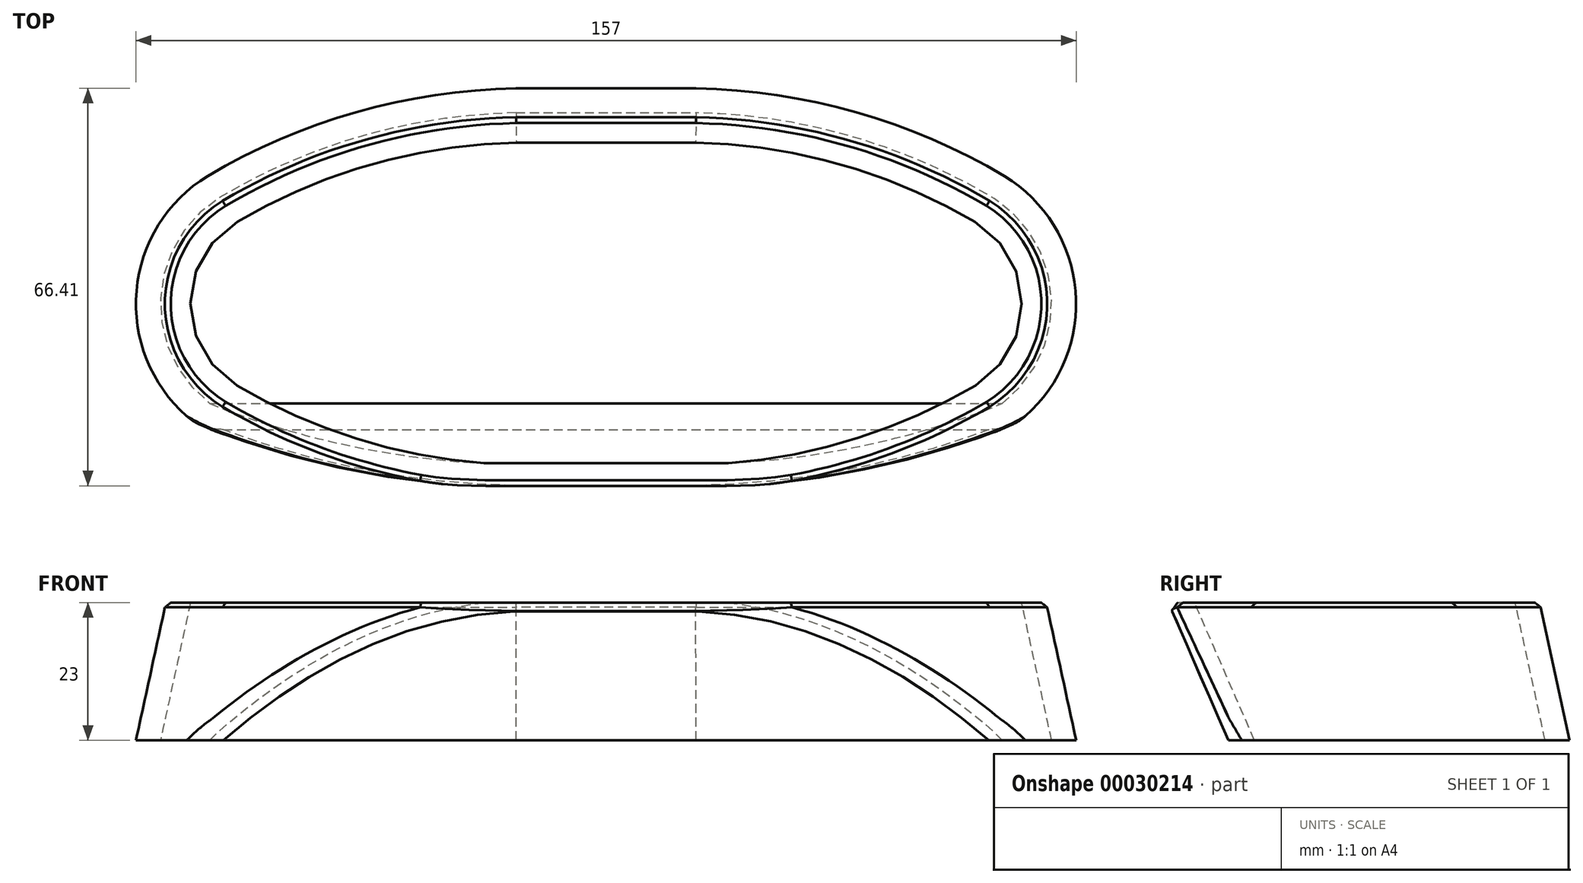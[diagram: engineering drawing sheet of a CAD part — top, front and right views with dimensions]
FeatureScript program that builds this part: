
annotation { "Feature Type Name" : "Feature", "Feature Type Description" : "" }
export const myFeature = defineFeature(function(context is Context, id is Id, definition is map)
    precondition{}
    {
        {
            var Q0;
            Q0=qCreatedBy(makeId("Top.planeOp"),FACE);
            var sketch = newSketch(context, id + "F0", { "sketchPlane" : qUnion([Q0])});
            skLineSegment(sketch, "E0.rect.bottom", {"start": v(-15, -31) * mm, "end": v(15, -31) * mm, "construction": true});
            skLineSegment(sketch, "E0.rect.top", {"start": v(-15, 31) * mm, "end": v(15, 31) * mm, "construction": true});
            skLineSegment(sketch, "E0.rect.left", {"start": v(-15, -31) * mm, "end": v(-15, 31) * mm, "construction": true});
            skLineSegment(sketch, "E0.rect.right", {"start": v(15, -31) * mm, "end": v(15, 31) * mm, "construction": true});
            skPoint(sketch, "E0.rect.middle", {"position": v(0, 0) * mm});
            skLineSegment(sketch, "E1", {"start": v(-53.5, 0) * mm, "end": v(0, 0) * mm, "construction": true});
            skArc(sketch, "E2", {"start": v(-63.95, 17.05) * mm, "mid": v(-73.5, 0) * mm, "end": v(-63.95, -17.05) * mm, "construction": true});
            skLineSegment(sketch, "E3", {"start": v(-15, 31) * mm, "end": v(-58.67, 19.32) * mm, "construction": true});
            skArc(sketch, "E4", {"start": v(-63.95, -17.05) * mm, "mid": v(-40.38, -27.2) * mm, "end": v(-15, -31) * mm, "construction": true});
            skArc(sketch, "E5.MirrorCS", {"start": v(-63.95, 17.05) * mm, "mid": v(-40.38, 27.2) * mm, "end": v(-15, 31) * mm, "construction": true});
            skArc(sketch, "E6.MirrorCS", {"start": v(63.95, 17.05) * mm, "mid": v(40.38, 27.2) * mm, "end": v(15, 31) * mm, "construction": true});
            skArc(sketch, "E7.MirrorCS", {"start": v(63.95, 17.05) * mm, "mid": v(73.5, 0) * mm, "end": v(63.95, -17.05) * mm, "construction": true});
            skArc(sketch, "E8.MirrorCS", {"start": v(63.95, -17.05) * mm, "mid": v(40.38, -27.2) * mm, "end": v(15, -31) * mm, "construction": true});
            skArc(sketch, "E9.0", {"start": v(-66.53, 21.34) * mm, "mid": v(-78.5, 0) * mm, "end": v(-66.53, -21.34) * mm});
            skArc(sketch, "E9.1", {"start": v(-66.53, -21.34) * mm, "mid": v(-41.74, -32) * mm, "end": v(-15.05, -36) * mm});
            skLineSegment(sketch, "E9.2", {"start": v(-15.05, -36) * mm, "end": v(15.05, -36) * mm});
            skArc(sketch, "E9.3", {"start": v(66.53, -21.34) * mm, "mid": v(41.74, -32) * mm, "end": v(15.05, -36) * mm});
            skArc(sketch, "E9.4", {"start": v(66.53, 21.34) * mm, "mid": v(78.5, 0) * mm, "end": v(66.53, -21.34) * mm});
            skArc(sketch, "E9.5", {"start": v(-66.53, 21.34) * mm, "mid": v(-41.74, 32) * mm, "end": v(-15.05, 36) * mm});
            skArc(sketch, "E9.6", {"start": v(66.53, 21.34) * mm, "mid": v(41.74, 32) * mm, "end": v(15.05, 36) * mm});
            skLineSegment(sketch, "E9.7", {"start": v(-15.05, 36) * mm, "end": v(15.05, 36) * mm});
            skSolve(sketch);
        }
        {
            var Q0;
            Q0=qCreatedBy(makeId("Top.planeOp"),FACE);
            cPlane(context, id + "F1", {"entities" : qUnion([Q0]), "cplaneType" : CPlaneType.OFFSET, "offset" : 23 * mm, "width" : 150 * mm, "height" : 150 * mm});
        }
        {
            var Q0;
            Q0=qCreatedBy(id+"F1.planeOp",FACE);
            var sketch = newSketch(context, id + "F2", { "sketchPlane" : qUnion([Q0])});
            skLineSegment(sketch, "E10.rect.bottom", {"start": v(-15, -31) * mm, "end": v(15, -31) * mm});
            skLineSegment(sketch, "E10.rect.top", {"start": v(-15, 31) * mm, "end": v(15, 31) * mm});
            skLineSegment(sketch, "E10.rect.left", {"start": v(-15, -31) * mm, "end": v(-15, 31) * mm, "construction": true});
            skLineSegment(sketch, "E10.rect.right", {"start": v(15, -31) * mm, "end": v(15, 31) * mm, "construction": true});
            skPoint(sketch, "E10.rect.middle", {"position": v(0, 0) * mm});
            skLineSegment(sketch, "E11", {"start": v(-53.5, 0) * mm, "end": v(0, 0) * mm, "construction": true});
            skArc(sketch, "E12", {"start": v(-63.95, 17.05) * mm, "mid": v(-73.5, 0) * mm, "end": v(-63.95, -17.05) * mm});
            skLineSegment(sketch, "E13", {"start": v(-15, 31) * mm, "end": v(-58.67, 19.32) * mm, "construction": true});
            skArc(sketch, "E14", {"start": v(-63.95, -17.05) * mm, "mid": v(-40.38, -27.2) * mm, "end": v(-15, -31) * mm});
            skArc(sketch, "E15.MirrorCS", {"start": v(-63.95, 17.05) * mm, "mid": v(-40.38, 27.2) * mm, "end": v(-15, 31) * mm});
            skArc(sketch, "E16.MirrorCS", {"start": v(63.95, 17.05) * mm, "mid": v(40.38, 27.2) * mm, "end": v(15, 31) * mm});
            skArc(sketch, "E17.MirrorCS", {"start": v(63.95, 17.05) * mm, "mid": v(73.5, 0) * mm, "end": v(63.95, -17.05) * mm});
            skArc(sketch, "E18.MirrorCS", {"start": v(63.95, -17.05) * mm, "mid": v(40.38, -27.2) * mm, "end": v(15, -31) * mm});
            skSolve(sketch);
        }
        {
            var Q0;
            Q0=makeQuery(id+"F0.imprint","IMPRINT",FACE,{"disambiguationData":[TD([[makeQuery(id+"F0.imprint","IMPRINT",EDGE,{"derivedFrom":sQuery(id+"F0.wireOp",EDGE,"E9.0")}),1.0]])]});
            var Q1;
            Q1=makeQuery(id+"F2.imprint","IMPRINT",FACE,{"disambiguationData":[TD([[makeQuery(id+"F2.imprint","IMPRINT",EDGE,{"derivedFrom":sQuery(id+"F2.wireOp",EDGE,"E10.rect.bottom")}),1.0]])]});
            loft(context, id + "F3", {"sheetProfilesArray" : [{ "sheetProfileEntities" : qUnion([Q0]) }, { "sheetProfileEntities" : qUnion([Q1]) }]});
        }
        {
            var Q0;
            Q0=qCreatedBy(makeId("Right.planeOp"),FACE);
            var sketch = newSketch(context, id + "F4", { "sketchPlane" : qUnion([Q0])});
            skLineSegment(sketch, "E19", {"start": v(-31, 23) * mm, "end": v(-21, 0) * mm});
            skLineSegment(sketch, "E20", {"start": v(-21, 0) * mm, "end": v(-51, 0) * mm});
            skLineSegment(sketch, "E21", {"start": v(-51, 0) * mm, "end": v(-31, 23) * mm});
            skSolve(sketch);
        }
        {
            var Q0;
            Q0 = qSketchRegion(id + "F4", true);
            extrude(context, id + "F5", {"entities" : qUnion([Q0]), "operationType" : NewBodyOperationType.REMOVE, "oppositeDirection" : true, "depth" : 70 * mm, "hasSecondDirection" : true, "secondDirectionOppositeDirection" : false, "secondDirectionDepth" : 70 * mm});
        }
        {
            var Q0;
            Q0=makeQuery(id+"F3.opLoft","CAP_FACE",FACE,{"disambiguationData":[OSD([makeQuery(id+"F2.imprint","IMPRINT",FACE,{"disambiguationData":[TD([[makeQuery(id+"F2.imprint","IMPRINT",EDGE,{"derivedFrom":sQuery(id+"F2.wireOp",EDGE,"E10.rect.bottom")}),1.0]])]})])],"isStart":true});
            var Q1;
            Q1=makeQuery(id+"F3.opLoft","CAP_FACE",FACE,{"disambiguationData":[OSD([makeQuery(id+"F0.imprint","IMPRINT",FACE,{"disambiguationData":[TD([[makeQuery(id+"F0.imprint","IMPRINT",EDGE,{"derivedFrom":sQuery(id+"F0.wireOp",EDGE,"E9.0")}),1.0]])]})])],"isStart":true});
            shell(context, id + "F6", {"entities" : qUnion([Q0, Q1]), "thickness" : 4 * mm});
        }
        {
            var Q0;
            Q0=makeQuery(id+"F5.boolean.opBoolean","INTERSECT",EDGE,{"derivedFrom":[makeQuery(id+"F3.opLoft","SWEPT_FACE",FACE,{"disambiguationData":[OSD([sQuery(id+"F0.wireOp",EDGE,"E9.0"),sQuery(id+"F0.wireOp",EDGE,"E9.1"),sQuery(id+"F0.wireOp",EDGE,"E9.2"),sQuery(id+"F2.wireOp",EDGE,"E10.rect.bottom"),sQuery(id+"F2.wireOp",EDGE,"E12"),sQuery(id+"F2.wireOp",EDGE,"E14")])]}),makeQuery(id+"F5.opExtrude","SWEPT_FACE",FACE,{"disambiguationData":[OSD([sQuery(id+"F4.wireOp",EDGE,"E19")])]})]});
            var Q1;
            Q1=makeQuery(id+"F5.boolean.opBoolean","INTERSECT",EDGE,{"derivedFrom":[makeQuery(id+"F3.opLoft","SWEPT_FACE",FACE,{"disambiguationData":[OSD([sQuery(id+"F0.wireOp",EDGE,"E9.2"),sQuery(id+"F0.wireOp",EDGE,"E9.3"),sQuery(id+"F0.wireOp",EDGE,"E9.4"),sQuery(id+"F2.wireOp",EDGE,"E10.rect.bottom"),sQuery(id+"F2.wireOp",EDGE,"E17.MirrorCS"),sQuery(id+"F2.wireOp",EDGE,"E18.MirrorCS")])]}),makeQuery(id+"F5.opExtrude","SWEPT_FACE",FACE,{"disambiguationData":[OSD([sQuery(id+"F4.wireOp",EDGE,"E19")])]})]});
            fillet(context, id + "F7", {"entities" : qUnion([Q0, Q1]), "radius" : 5 * mm, "tangentPropagation" : true, "allowEdgeOverflow" : false});
        }
        {
            var Q0;
            Q0=makeQuery(id+"F3.opLoft","MID_CAP_EDGE",EDGE,{"disambiguationData":[OSD([sQuery(id+"F2.wireOp",EDGE,"E10.rect.top"),sQuery(id+"F2.wireOp",EDGE,"E12"),sQuery(id+"F2.wireOp",EDGE,"E15.MirrorCS")])],"capPos":1.0});
            var Q1;
            Q1=makeQuery(id+"F3.opLoft","MID_CAP_EDGE",EDGE,{"disambiguationData":[OSD([sQuery(id+"F2.wireOp",EDGE,"E12"),sQuery(id+"F2.wireOp",EDGE,"E14"),sQuery(id+"F2.wireOp",EDGE,"E15.MirrorCS")])],"capPos":1.0});
            var Q2;
            Q2=makeQuery(id+"F3.opLoft","MID_CAP_EDGE",EDGE,{"disambiguationData":[OSD([sQuery(id+"F2.wireOp",EDGE,"E10.rect.bottom"),sQuery(id+"F2.wireOp",EDGE,"E12"),sQuery(id+"F2.wireOp",EDGE,"E14")])],"capPos":1.0});
            var Q3;
            {var subQ0=sQuery(id+"F2.wireOp",EDGE,"E10.rect.bottom");var subQ1=sQuery(id+"F2.wireOp",EDGE,"E12");var subQ2=sQuery(id+"F2.wireOp",EDGE,"E14");Q3=makeQuery(id+"F7.opFillet","BLEND_EDGE",EDGE,{"blendedFrom":[makeQuery(id+"F5.boolean.opBoolean","INTERSECT",EDGE,{"derivedFrom":[makeQuery(id+"F3.opLoft","SWEPT_FACE",FACE,{"disambiguationData":[OSD([sQuery(id+"F0.wireOp",EDGE,"E9.0"),sQuery(id+"F0.wireOp",EDGE,"E9.1"),sQuery(id+"F0.wireOp",EDGE,"E9.2"),subQ0,subQ1,subQ2])]}),makeQuery(id+"F5.opExtrude","SWEPT_FACE",FACE,{"disambiguationData":[OSD([sQuery(id+"F4.wireOp",EDGE,"E19")])]})]}),makeQuery(id+"F3.opLoft","CAP_FACE",FACE,{"disambiguationData":[OSD([makeQuery(id+"F2.imprint","IMPRINT",FACE,{"disambiguationData":[TD([[makeQuery(id+"F2.imprint","IMPRINT",EDGE,{"derivedFrom":subQ0}),1.0]])]})])],"isStart":true})],"blendedInto":[makeQuery(id+"F3.opLoft","CAP_FACE",FACE,{"disambiguationData":[OSD([makeQuery(id+"F2.imprint","IMPRINT",FACE,{"disambiguationData":[TD([[makeQuery(id+"F2.imprint","IMPRINT",EDGE,{"derivedFrom":subQ0}),1.0]])]})])],"isStart":true})]});}
            var Q4;
            {var subQ0=sQuery(id+"F2.wireOp",EDGE,"E10.rect.bottom");var subQ1=sQuery(id+"F2.wireOp",EDGE,"E17.MirrorCS");var subQ2=sQuery(id+"F2.wireOp",EDGE,"E18.MirrorCS");Q4=makeQuery(id+"F7.opFillet","BLEND_EDGE",EDGE,{"blendedFrom":[makeQuery(id+"F5.boolean.opBoolean","INTERSECT",EDGE,{"derivedFrom":[makeQuery(id+"F3.opLoft","SWEPT_FACE",FACE,{"disambiguationData":[OSD([sQuery(id+"F0.wireOp",EDGE,"E9.2"),sQuery(id+"F0.wireOp",EDGE,"E9.3"),sQuery(id+"F0.wireOp",EDGE,"E9.4"),subQ0,subQ1,subQ2])]}),makeQuery(id+"F5.opExtrude","SWEPT_FACE",FACE,{"disambiguationData":[OSD([sQuery(id+"F4.wireOp",EDGE,"E19")])]})]}),makeQuery(id+"F3.opLoft","CAP_FACE",FACE,{"disambiguationData":[OSD([makeQuery(id+"F2.imprint","IMPRINT",FACE,{"disambiguationData":[TD([[makeQuery(id+"F2.imprint","IMPRINT",EDGE,{"derivedFrom":subQ0}),1.0]])]})])],"isStart":true})],"blendedInto":[makeQuery(id+"F3.opLoft","CAP_FACE",FACE,{"disambiguationData":[OSD([makeQuery(id+"F2.imprint","IMPRINT",FACE,{"disambiguationData":[TD([[makeQuery(id+"F2.imprint","IMPRINT",EDGE,{"derivedFrom":subQ0}),1.0]])]})])],"isStart":true})]});}
            var Q5;
            Q5=makeQuery(id+"F3.opLoft","MID_CAP_EDGE",EDGE,{"disambiguationData":[OSD([sQuery(id+"F2.wireOp",EDGE,"E10.rect.bottom"),sQuery(id+"F2.wireOp",EDGE,"E17.MirrorCS"),sQuery(id+"F2.wireOp",EDGE,"E18.MirrorCS")])],"capPos":1.0});
            var Q6;
            Q6=makeQuery(id+"F3.opLoft","MID_CAP_EDGE",EDGE,{"disambiguationData":[OSD([sQuery(id+"F2.wireOp",EDGE,"E16.MirrorCS"),sQuery(id+"F2.wireOp",EDGE,"E17.MirrorCS"),sQuery(id+"F2.wireOp",EDGE,"E18.MirrorCS")])],"capPos":1.0});
            var Q7;
            Q7=makeQuery(id+"F3.opLoft","MID_CAP_EDGE",EDGE,{"disambiguationData":[OSD([sQuery(id+"F2.wireOp",EDGE,"E10.rect.top"),sQuery(id+"F2.wireOp",EDGE,"E16.MirrorCS"),sQuery(id+"F2.wireOp",EDGE,"E17.MirrorCS")])],"capPos":1.0});
            var Q8;
            Q8=makeQuery(id+"F3.opLoft","MID_CAP_EDGE",EDGE,{"disambiguationData":[OSD([sQuery(id+"F2.wireOp",EDGE,"E10.rect.top"),sQuery(id+"F2.wireOp",EDGE,"E15.MirrorCS"),sQuery(id+"F2.wireOp",EDGE,"E16.MirrorCS")])],"capPos":1.0});
            chamfer(context, id + "F8", {"entities" : qUnion([Q0, Q1, Q2, Q3, Q4, Q5, Q6, Q7, Q8]), "width" : 1 * mm, "tangentPropagation" : true});
        }
    });
